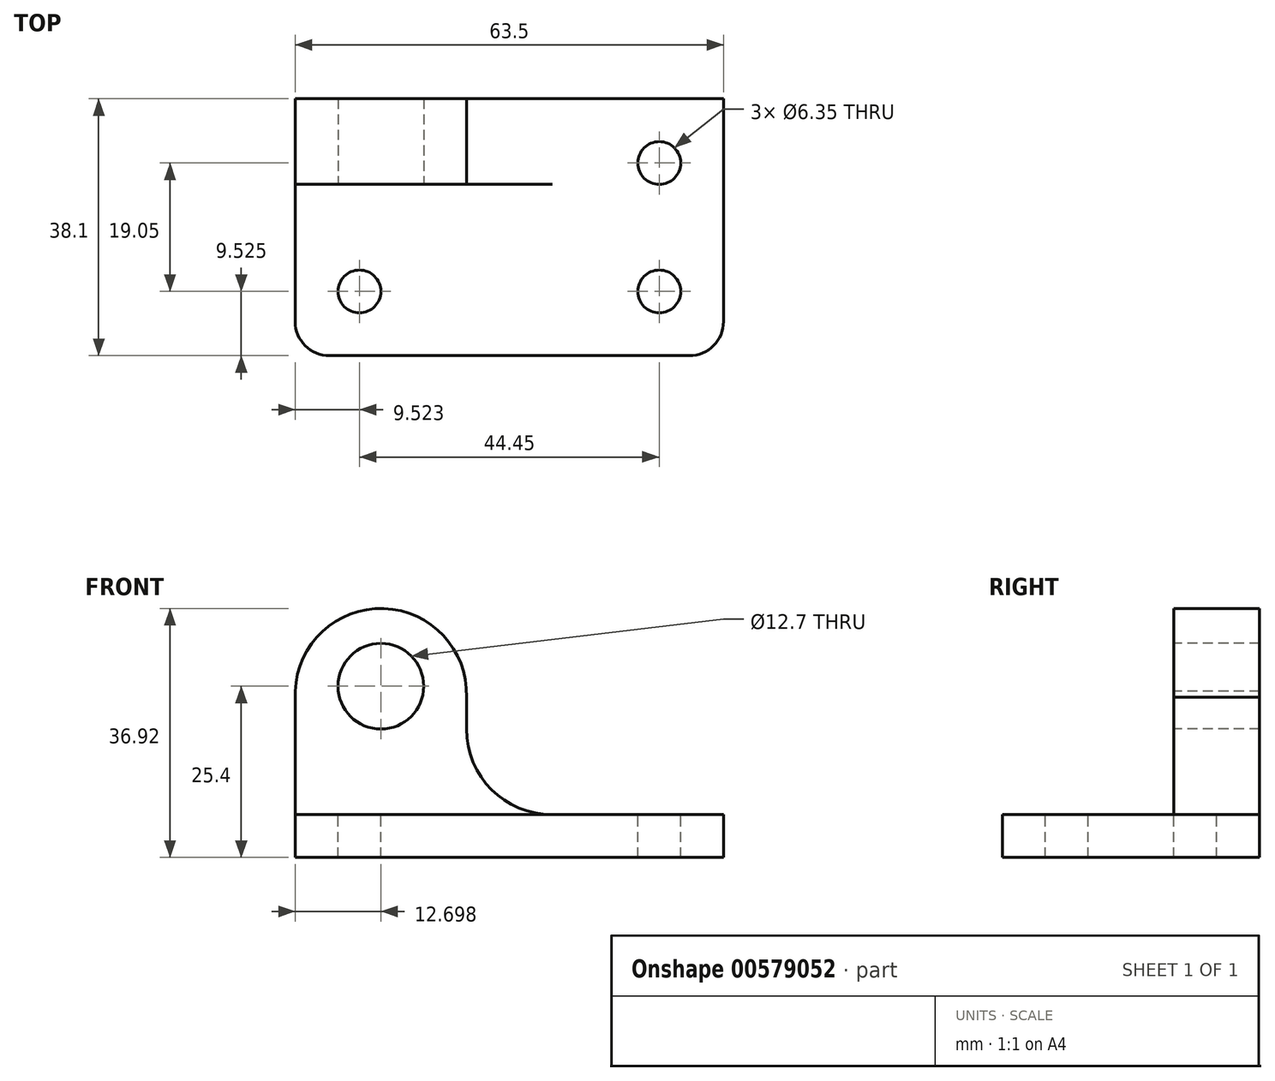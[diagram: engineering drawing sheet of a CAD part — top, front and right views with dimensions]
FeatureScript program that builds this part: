
annotation { "Feature Type Name" : "Feature", "Feature Type Description" : "" }
export const myFeature = defineFeature(function(context is Context, id is Id, definition is map)
    precondition{}
    {
        {
            var Q0;
            Q0=qCreatedBy(makeId("Front.planeOp"),FACE);
            var sketch = newSketch(context, id + "F0", { "sketchPlane" : qUnion([Q0])});
            skLineSegment(sketch, "E0", {"start": v(-53.2, 53.47) * mm, "end": v(-53.2, 15.37) * mm});
            skLineSegment(sketch, "E1", {"start": v(-53.2, 15.37) * mm, "end": v(10.3, 15.37) * mm});
            skLineSegment(sketch, "E2", {"start": v(10.3, 15.37) * mm, "end": v(10.3, 21.72) * mm});
            skLineSegment(sketch, "E3", {"start": v(10.3, 21.72) * mm, "end": v(-15.1, 21.72) * mm});
            skLineSegment(sketch, "E4", {"start": v(-15.1, 21.72) * mm, "end": v(-15.1, 53.47) * mm});
            skLineSegment(sketch, "E5", {"start": v(-15.1, 53.47) * mm, "end": v(-53.2, 53.47) * mm});
            skSolve(sketch);
        }
        {
            var Q0;
            Q0=makeQuery(id+"F0.imprint","IMPRINT",FACE,{"disambiguationData":[TD([[makeQuery(id+"F0.imprint","IMPRINT",EDGE,{"derivedFrom":sQuery(id+"F0.wireOp",EDGE,"E0")}),1.0]])]});
            var sketch = newSketch(context, id + "F1", { "sketchPlane" : qUnion([Q0])});
            skSolve(sketch);
        }
        {
            var Q0;
            Q0 = qSketchRegion(id + "F1", true);
            var Q1;
            Q1=makeQuery(id+"F0.imprint","IMPRINT",FACE,{"disambiguationData":[TD([[makeQuery(id+"F0.imprint","IMPRINT",EDGE,{"derivedFrom":sQuery(id+"F0.wireOp",EDGE,"E0")}),1.0]])]});
            extrude(context, id + "F2", {"entities" : qUnion([Q0, Q1]), "depth" : 38.1 * mm, "offsetDistance" : 25.4 * mm});
        }
        {
            var Q0;
            Q0=makeQuery(id+"F2.opExtrude","SWEPT_FACE",FACE,{"disambiguationData":[OSD([sQuery(id+"F0.wireOp",EDGE,"E4")])]});
            var sketch = newSketch(context, id + "F3", { "sketchPlane" : qUnion([Q0])});
            skLineSegment(sketch, "E6", {"start": v(-12.7, 53.47) * mm, "end": v(-12.7, 21.72) * mm});
            skLineSegment(sketch, "E7", {"start": v(-12.7, 21.72) * mm, "end": v(-38.1, 21.72) * mm});
            skSolve(sketch);
        }
        {
            var Q0;
            {var subQ0=sQuery(id+"F3.wireOp",EDGE,"E6");Q0=makeQuery(id+"F3.imprint","IMPRINT",FACE,{"disambiguationData":[TD([[makeQuery(id+"F3.imprint","IMPRINT",EDGE,{"derivedFrom":subQ0}),-1.0]])]});}
            extrude(context, id + "F4", {"entities" : qUnion([Q0]), "operationType" : NewBodyOperationType.REMOVE, "oppositeDirection" : true, "depth" : 25.4 * mm, "offsetDistance" : 25.4 * mm});
        }
        {
            var Q0;
            Q0=makeQuery(id+"F4.boolean.opBoolean","COPY",FACE,{"derivedFrom":makeQuery(id+"F4.opExtrude","CAP_FACE",FACE,{"disambiguationData":[OSD([sQuery(id+"F0.wireOp",EDGE,"E4"),sQuery(id+"F0.wireOp",EDGE,"E5"),sQuery(id+"F3.wireOp",EDGE,"E6"),sQuery(id+"F3.wireOp",EDGE,"E7")])],"isStart":false})});
            extrude(context, id + "F5", {"entities" : qUnion([Q0]), "operationType" : NewBodyOperationType.REMOVE, "oppositeDirection" : true, "depth" : 12.7 * mm, "offsetDistance" : 25.4 * mm});
        }
        {
            var Q0;
            {var subQ0=sQuery(id+"F3.wireOp",EDGE,"E6");Q0=makeQuery(id+"F5.boolean.opBoolean","MERGE",FACE,{"derivedFrom":[makeQuery(id+"F4.boolean.opBoolean","COPY",FACE,{"derivedFrom":makeQuery(id+"F4.opExtrude","SWEPT_FACE",FACE,{"disambiguationData":[OSD([subQ0])]})}),makeQuery(id+"F5.opExtrude","SWEPT_FACE",FACE,{"disambiguationData":[OSD([subQ0])]})]});}
            var sketch = newSketch(context, id + "F6", { "sketchPlane" : qUnion([Q0])});
            skCircle(sketch, "E8", {"center": v(-40.5, 40.77) * mm, "radius": 6.35 * mm});
            skSolve(sketch);
        }
        {
            var Q0;
            Q0=sQuery(id+"F6.wireOp",VERTEX,"E8.center");
            var Q1;
            Q1=makeQuery(id+"F2.opExtrude","SWEPT_BODY",BODY,{"disambiguationData":[OSD([sQuery(id+"F0.wireOp",EDGE,"E0"),sQuery(id+"F0.wireOp",EDGE,"E1"),sQuery(id+"F0.wireOp",EDGE,"E2"),sQuery(id+"F0.wireOp",EDGE,"E3"),sQuery(id+"F0.wireOp",EDGE,"E4"),sQuery(id+"F0.wireOp",EDGE,"E5")])]});
            hole(context, id + "F7", {"style" : HoleStyle.SIMPLE, "endStyle" : HoleEndStyle.THROUGH, "holeDiameter" : 12.7 * mm, "majorDiameter" : 6.35 * mm, "isTappedThrough" : true, "tappedDepth" : 12.7 * mm, "tapClearance" : 3, "locations" : qUnion([Q0]), "scope" : qUnion([Q1])});
        }
        {
            var Q0;
            {var subQ0=sQuery(id+"F3.wireOp",EDGE,"E6");Q0=makeQuery(id+"F5.boolean.opBoolean","MERGE",FACE,{"derivedFrom":[makeQuery(id+"F4.boolean.opBoolean","COPY",FACE,{"derivedFrom":makeQuery(id+"F4.opExtrude","SWEPT_FACE",FACE,{"disambiguationData":[OSD([subQ0])]})}),makeQuery(id+"F5.opExtrude","SWEPT_FACE",FACE,{"disambiguationData":[OSD([subQ0])]})]});}
            var sketch = newSketch(context, id + "F8", { "sketchPlane" : qUnion([Q0])});
            skArc(sketch, "E9", {"start": v(-27.8, 39.16) * mm, "mid": v(-40.06, 52.28) * mm, "end": v(-53.2, 40.03) * mm});
            skArc(sketch, "E10", {"start": v(-27.8, 34.42) * mm, "mid": v(-24.08, 25.44) * mm, "end": v(-15.1, 21.72) * mm});
            skLineSegment(sketch, "E11", {"start": v(-27.8, 39.16) * mm, "end": v(-27.8, 34.42) * mm});
            skSolve(sketch);
        }
        {
            var Q0;
            {var subQ1=sQuery(id+"F8.wireOp",EDGE,"E9");Q0=makeQuery(id+"F8.imprint","IMPRINT",FACE,{"disambiguationData":[TD([[makeQuery(id+"F8.imprint","IMPRINT",EDGE,{"derivedFrom":subQ1}),-1.0]])]});}
            extrude(context, id + "F9", {"entities" : qUnion([Q0]), "operationType" : NewBodyOperationType.REMOVE, "oppositeDirection" : true, "depth" : 12.7 * mm, "offsetDistance" : 25.4 * mm});
        }
        {
            var Q0;
            Q0=makeQuery(id+"F1.imprint","IMPRINT",FACE,{"disambiguationData":[TD([[makeQuery(id+"F1.imprint","IMPRINT",EDGE,{"derivedFrom":makeQuery(id+"F0.imprint","IMPRINT",EDGE,{"derivedFrom":sQuery(id+"F0.wireOp",EDGE,"E0")})}),1.0]])]});
            extrude(context, id + "F10", {"entities" : qUnion([Q0]), "operationType" : NewBodyOperationType.REMOVE, "endBound" : BoundingType.THROUGH_ALL, "oppositeDirection" : true, "depth" : 25.4 * mm, "offsetDistance" : 25.4 * mm});
        }
        {
            var Q0;
            Q0=makeQuery(id+"F2.opExtrude","CAP_EDGE",EDGE,{"disambiguationData":[OSD([sQuery(id+"F0.wireOp",EDGE,"E0")])],"isStart":false});
            var Q1;
            Q1=makeQuery(id+"F2.opExtrude","CAP_EDGE",EDGE,{"disambiguationData":[OSD([sQuery(id+"F0.wireOp",EDGE,"E2")])],"isStart":false});
            fillet(context, id + "F11", {"entities" : qUnion([Q0, Q1]), "radius" : 5.08 * mm, "tangentPropagation" : true, "allowEdgeOverflow" : false});
        }
        {
            var Q0;
            {var subQ0=sQuery(id+"F3.wireOp",EDGE,"E7");Q0=makeQuery(id+"F5.boolean.opBoolean","MERGE",FACE,{"derivedFrom":[makeQuery(id+"F4.boolean.opBoolean","MERGE",FACE,{"derivedFrom":[makeQuery(id+"F2.opExtrude","SWEPT_FACE",FACE,{"disambiguationData":[OSD([sQuery(id+"F0.wireOp",EDGE,"E3")])]}),makeQuery(id+"F4.opExtrude","SWEPT_FACE",FACE,{"disambiguationData":[OSD([subQ0])]})]}),makeQuery(id+"F5.opExtrude","SWEPT_FACE",FACE,{"disambiguationData":[OSD([subQ0])]})]});}
            var sketch = newSketch(context, id + "F12", { "sketchPlane" : qUnion([Q0])});
            skCircle(sketch, "E12", {"center": v(-43.67, -28.58) * mm, "radius": 3.18 * mm});
            skSolve(sketch);
        }
        {
            var Q0;
            Q0=sQuery(id+"F12.wireOp",VERTEX,"E12.center");
            var Q1;
            Q1=makeQuery(id+"F2.opExtrude","SWEPT_BODY",BODY,{"disambiguationData":[OSD([sQuery(id+"F0.wireOp",EDGE,"E0"),sQuery(id+"F0.wireOp",EDGE,"E1"),sQuery(id+"F0.wireOp",EDGE,"E2"),sQuery(id+"F0.wireOp",EDGE,"E3"),sQuery(id+"F0.wireOp",EDGE,"E4"),sQuery(id+"F0.wireOp",EDGE,"E5")])]});
            hole(context, id + "F13", {"style" : HoleStyle.SIMPLE, "endStyle" : HoleEndStyle.THROUGH, "holeDiameter" : 6.35 * mm, "majorDiameter" : 6.35 * mm, "isTappedThrough" : true, "tappedDepth" : 12.7 * mm, "tapClearance" : 3, "locations" : qUnion([Q0]), "scope" : qUnion([Q1])});
        }
        {
            var Q0;
            {var subQ0=sQuery(id+"F3.wireOp",EDGE,"E7");Q0=makeQuery(id+"F5.boolean.opBoolean","MERGE",FACE,{"derivedFrom":[makeQuery(id+"F4.boolean.opBoolean","MERGE",FACE,{"derivedFrom":[makeQuery(id+"F2.opExtrude","SWEPT_FACE",FACE,{"disambiguationData":[OSD([sQuery(id+"F0.wireOp",EDGE,"E3")])]}),makeQuery(id+"F4.opExtrude","SWEPT_FACE",FACE,{"disambiguationData":[OSD([subQ0])]})]}),makeQuery(id+"F5.opExtrude","SWEPT_FACE",FACE,{"disambiguationData":[OSD([subQ0])]})]});}
            var sketch = newSketch(context, id + "F14", { "sketchPlane" : qUnion([Q0])});
            skCircle(sketch, "E13", {"center": v(0.78, -9.52) * mm, "radius": 3.18 * mm});
            skSolve(sketch);
        }
        {
            var Q0;
            Q0=sQuery(id+"F14.wireOp",VERTEX,"E13.center");
            var Q1;
            Q1=makeQuery(id+"F2.opExtrude","SWEPT_BODY",BODY,{"disambiguationData":[OSD([sQuery(id+"F0.wireOp",EDGE,"E0"),sQuery(id+"F0.wireOp",EDGE,"E1"),sQuery(id+"F0.wireOp",EDGE,"E2"),sQuery(id+"F0.wireOp",EDGE,"E3"),sQuery(id+"F0.wireOp",EDGE,"E4"),sQuery(id+"F0.wireOp",EDGE,"E5")])]});
            hole(context, id + "F15", {"style" : HoleStyle.SIMPLE, "endStyle" : HoleEndStyle.THROUGH, "holeDiameter" : 6.35 * mm, "majorDiameter" : 6.35 * mm, "isTappedThrough" : true, "tappedDepth" : 12.7 * mm, "tapClearance" : 3, "locations" : qUnion([Q0]), "scope" : qUnion([Q1])});
        }
        {
            var Q0;
            {var subQ0=sQuery(id+"F3.wireOp",EDGE,"E7");Q0=makeQuery(id+"F5.boolean.opBoolean","MERGE",FACE,{"derivedFrom":[makeQuery(id+"F4.boolean.opBoolean","MERGE",FACE,{"derivedFrom":[makeQuery(id+"F2.opExtrude","SWEPT_FACE",FACE,{"disambiguationData":[OSD([sQuery(id+"F0.wireOp",EDGE,"E3")])]}),makeQuery(id+"F4.opExtrude","SWEPT_FACE",FACE,{"disambiguationData":[OSD([subQ0])]})]}),makeQuery(id+"F5.opExtrude","SWEPT_FACE",FACE,{"disambiguationData":[OSD([subQ0])]})]});}
            var sketch = newSketch(context, id + "F16", { "sketchPlane" : qUnion([Q0])});
            skCircle(sketch, "E14", {"center": v(0.78, -28.58) * mm, "radius": 3.18 * mm});
            skSolve(sketch);
        }
        {
            var Q0;
            Q0=sQuery(id+"F16.wireOp",VERTEX,"E14.center");
            var Q1;
            Q1=makeQuery(id+"F2.opExtrude","SWEPT_BODY",BODY,{"disambiguationData":[OSD([sQuery(id+"F0.wireOp",EDGE,"E0"),sQuery(id+"F0.wireOp",EDGE,"E1"),sQuery(id+"F0.wireOp",EDGE,"E2"),sQuery(id+"F0.wireOp",EDGE,"E3"),sQuery(id+"F0.wireOp",EDGE,"E4"),sQuery(id+"F0.wireOp",EDGE,"E5")])]});
            hole(context, id + "F17", {"style" : HoleStyle.SIMPLE, "endStyle" : HoleEndStyle.THROUGH, "holeDiameter" : 6.35 * mm, "majorDiameter" : 6.35 * mm, "isTappedThrough" : true, "tappedDepth" : 12.7 * mm, "tapClearance" : 3, "locations" : qUnion([Q0]), "scope" : qUnion([Q1])});
        }
    });
